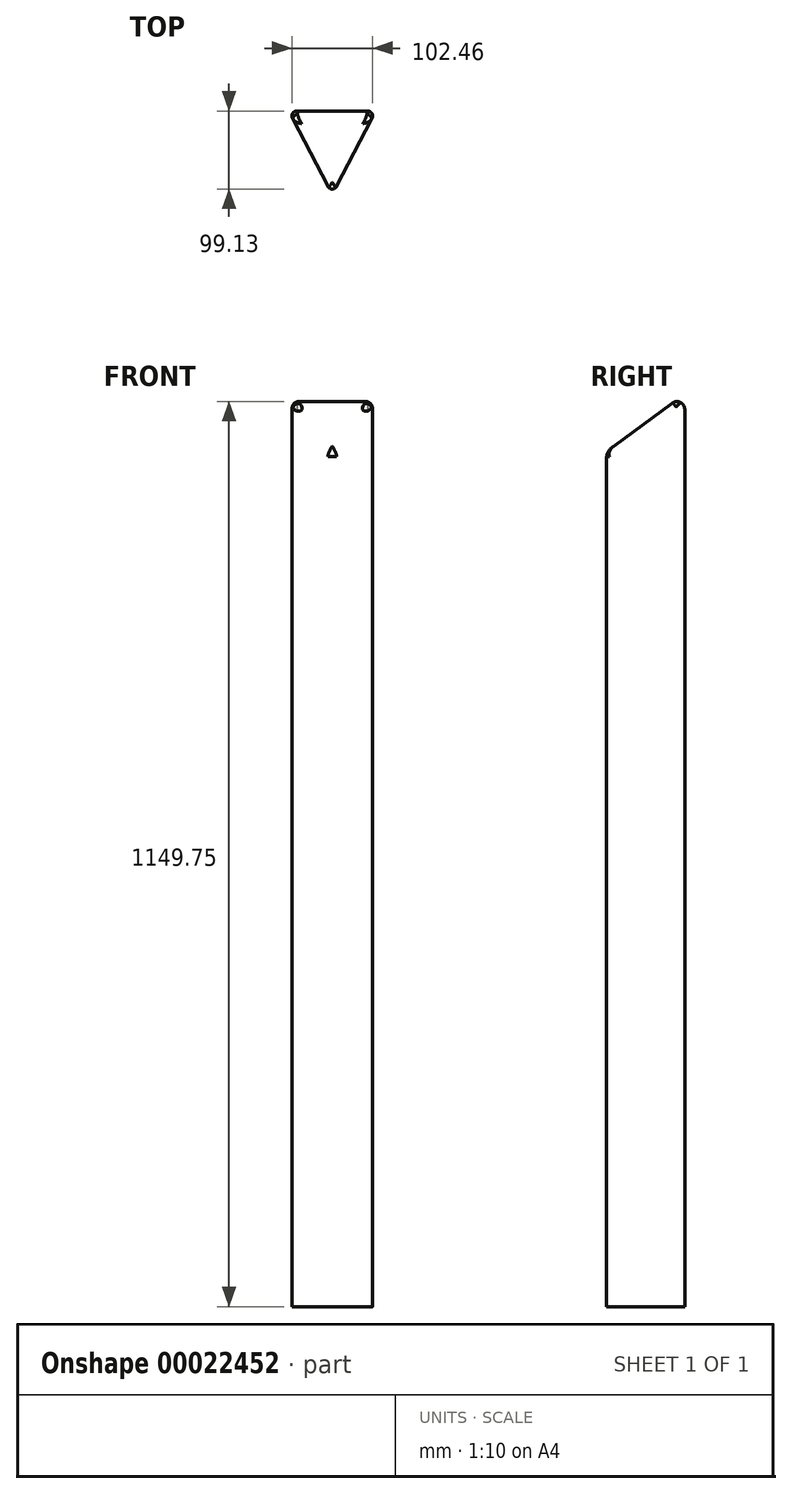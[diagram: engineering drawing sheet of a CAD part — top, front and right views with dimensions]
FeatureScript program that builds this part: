
annotation { "Feature Type Name" : "Feature", "Feature Type Description" : "" }
export const myFeature = defineFeature(function(context is Context, id is Id, definition is map)
    precondition{}
    {
        {
            var Q0;
            Q0=qCreatedBy(makeId("Top.planeOp"),FACE);
            var sketch = newSketch(context, id + "F0", { "sketchPlane" : qUnion([Q0])});
            skLineSegment(sketch, "E0", {"start": v(0, 48.2) * mm, "end": v(-44.88, 48.2) * mm});
            skLineSegment(sketch, "E1", {"start": v(-50.51, 38.92) * mm, "end": v(-5.64, -47.5) * mm});
            skPoint(sketch, "E2.visualSharp", {"position": v(-55.33, 48.2) * mm});
            skArc(sketch, "E2.filletArc", {"start": v(-44.88, 48.2) * mm, "mid": v(-50.3, 45.15) * mm, "end": v(-50.51, 38.92) * mm});
            skLineSegment(sketch, "E3.MirrorCS", {"start": v(0, 48.2) * mm, "end": v(44.88, 48.2) * mm});
            skArc(sketch, "E4.MirrorCS", {"start": v(44.88, 48.2) * mm, "mid": v(50.3, 45.15) * mm, "end": v(50.51, 38.92) * mm});
            skLineSegment(sketch, "E5.MirrorCS", {"start": v(50.51, 38.92) * mm, "end": v(5.64, -47.5) * mm});
            skPoint(sketch, "E6.visualSharp", {"position": v(0, -58.36) * mm});
            skArc(sketch, "E6.filletArc", {"start": v(-5.64, -47.5) * mm, "mid": v(0, -50.93) * mm, "end": v(5.64, -47.5) * mm});
            skSolve(sketch);
        }
        {
            var Q0;
            Q0 = qSketchRegion(id + "F0", true);
            extrude(context, id + "F1", {"entities" : qUnion([Q0]), "depth" : 1200 * mm});
        }
        {
            var Q0;
            Q0=qCreatedBy(makeId("Right.planeOp"),FACE);
            cPlane(context, id + "F2", {"entities" : qUnion([Q0]), "cplaneType" : CPlaneType.OFFSET, "offset" : 150 * mm, "width" : 150 * mm, "height" : 150 * mm});
        }
        {
            var Q0;
            Q0=qCreatedBy(id+"F2.planeOp",FACE);
            var sketch = newSketch(context, id + "F3", { "sketchPlane" : qUnion([Q0])});
            skLineSegment(sketch, "E7", {"start": v(-217.07, 964.2) * mm, "end": v(120.98, 1213.13) * mm});
            skLineSegment(sketch, "E8", {"start": v(120.98, 1213.13) * mm, "end": v(-134.97, 1213.13) * mm});
            skLineSegment(sketch, "E9", {"start": v(-134.97, 1213.13) * mm, "end": v(-217.07, 964.2) * mm});
            skSolve(sketch);
        }
        {
            var Q0;
            Q0=makeQuery(id+"F3.imprint","IMPRINT",FACE,{"disambiguationData":[TD([[makeQuery(id+"F3.imprint","IMPRINT",EDGE,{"derivedFrom":sQuery(id+"F3.wireOp",EDGE,"E7")}),1.0]])]});
            extrude(context, id + "F4", {"entities" : qUnion([Q0]), "operationType" : NewBodyOperationType.REMOVE, "oppositeDirection" : true, "depth" : 500 * mm});
        }
        {
            var Q0;
            Q0=makeQuery(id+"F4.boolean.opBoolean","INTERSECT",EDGE,{"derivedFrom":[makeQuery(id+"F1.opExtrude","SWEPT_FACE",FACE,{"disambiguationData":[OSD([sQuery(id+"F0.wireOp",EDGE,"E0"),sQuery(id+"F0.wireOp",EDGE,"E3.MirrorCS")])]}),makeQuery(id+"F4.opExtrude","SWEPT_FACE",FACE,{"disambiguationData":[OSD([sQuery(id+"F3.wireOp",EDGE,"E7")])]})]});
            fillet(context, id + "F5", {"entities" : qUnion([Q0]), "radius" : 10 * mm, "tangentPropagation" : true, "allowEdgeOverflow" : false});
        }
    });
